# Revit family: Gewindestift M10 links rechts
name_source: partatom
category: HLS-Bauteile
revit_build: Autodesk Revit 2017 (Build: 20190507_1515(x64)
units: mm (PartAtom-declared; Revit-internal decimal feet)

## family parameters
Arbeitsebenenbasiert = Ja
Beim Laden mit Abzugskörper schneiden = Nein
Bemaßung runder Anschluss = Durchmesser verwenden
Gemeinsam genutzt = Ja
Immer vertikal = Nein
Raumberechnungspunkt = Nein
Teiletyp = Normal

## types (1)
- Gewindestift L/R M10
    Artikelnummer = 08120770
    D = 7 mm  [stored 0.0229659 ft]
    EAN = 4250928459275
    Fabrikat = MEFA
    Festigkeitsklasse = 4.6
    Firma = MEFA Befestigungs- und Montagesysteme GmbH
    Gewicht = 0.02 kg
    Gewicht pro Bauteil = 0.02 kg
    Gewinde = M10
    Kurztext1 = Gewindestift links-rechts
    Kurztext2 = M10 x 60 mm gvz FK 4.6
    L = 60 mm  [stored 0.19685 ft]
    L2 = 4 mm  [stored 0.0131234 ft]
    L3 = 4 mm  [stored 0.0131234 ft]
    Länge = 60 mm  [stored 0.19685 ft]
    Länge Gewinde 1 = 25 mm
    Länge Gewinde 2 = 25 mm
    Material = Stahl
    Mengeneinheit = St
    Oberflaeche = galvanisch verzinkt
    Vorgabe-Ansicht = 1219 mm
    vpe = 10

note: [stored X ft] marks values corroborated as IEEE doubles in the binary element streams (Revit-internal decimal feet)
